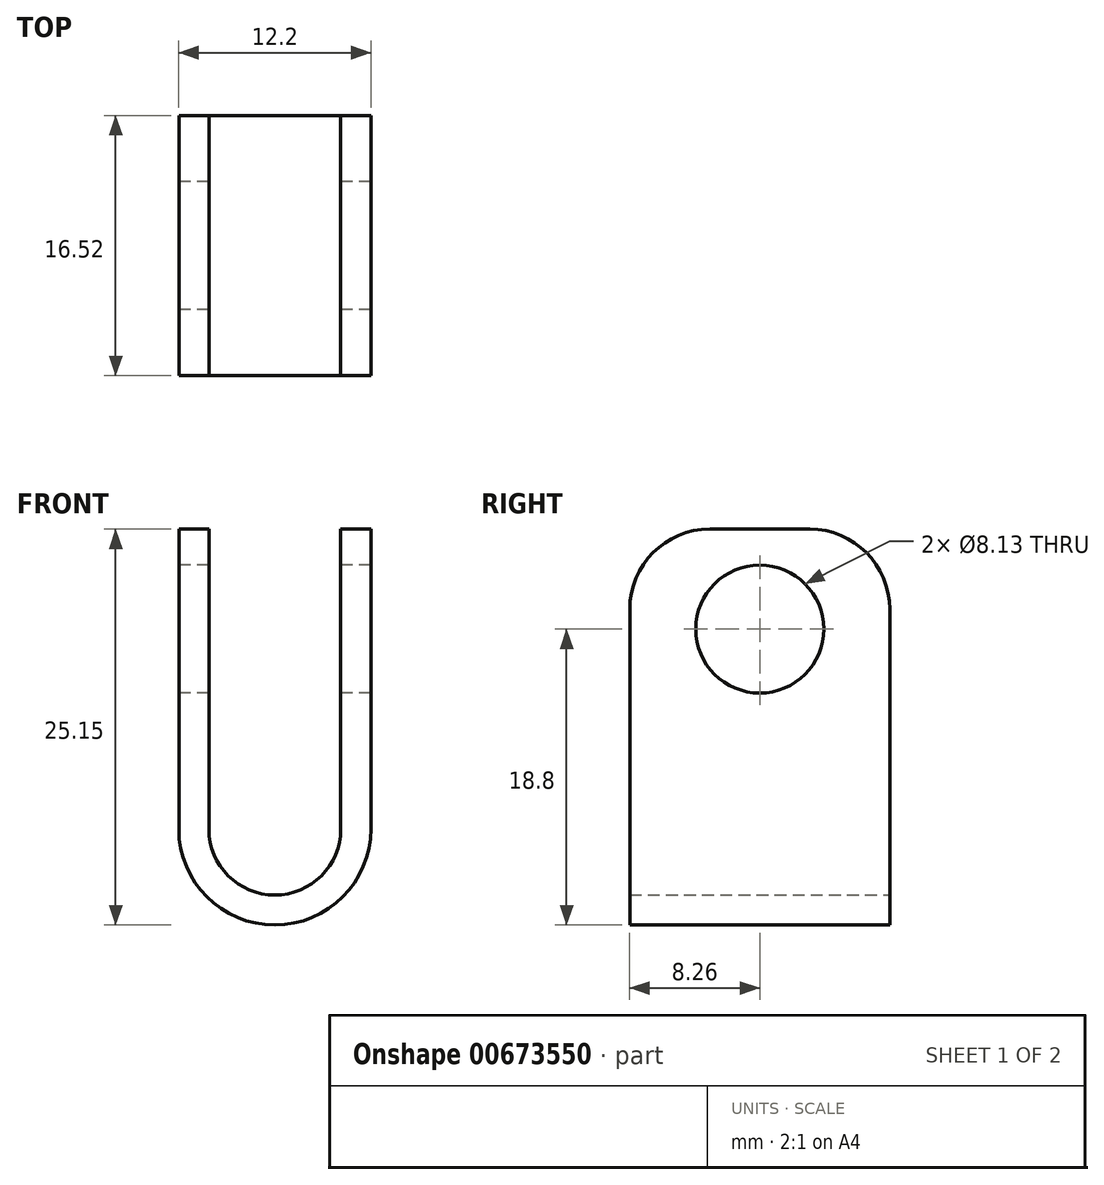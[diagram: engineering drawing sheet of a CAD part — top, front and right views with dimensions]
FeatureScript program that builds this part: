
annotation { "Feature Type Name" : "Feature", "Feature Type Description" : "" }
export const myFeature = defineFeature(function(context is Context, id is Id, definition is map)
    precondition{}
    {
        {
            var Q0;
            Q0=qCreatedBy(makeId("Front.planeOp"),FACE);
            var sketch = newSketch(context, id + "F0", { "sketchPlane" : qUnion([Q0])});
            skArc(sketch, "E0", {"start": v(-4.2, 0) * mm, "mid": v(0, -4.2) * mm, "end": v(4.2, 0) * mm});
            skArc(sketch, "E1", {"start": v(-6.1, 0) * mm, "mid": v(0, -6.1) * mm, "end": v(6.1, 0) * mm});
            skLineSegment(sketch, "E2", {"start": v(-6.1, 0) * mm, "end": v(-6.1, 19.05) * mm});
            skLineSegment(sketch, "E3", {"start": v(6.1, 19.05) * mm, "end": v(6.1, 0) * mm});
            skLineSegment(sketch, "E4", {"start": v(-4.2, 0) * mm, "end": v(-4.2, 19.05) * mm});
            skLineSegment(sketch, "E5", {"start": v(4.2, 0) * mm, "end": v(4.2, 19.05) * mm});
            skLineSegment(sketch, "E6", {"start": v(4.2, 19.05) * mm, "end": v(6.1, 19.05) * mm});
            skLineSegment(sketch, "E7", {"start": v(-6.1, 19.05) * mm, "end": v(-4.2, 19.05) * mm});
            skSolve(sketch);
        }
        {
            var Q0;
            Q0=qSketchRegion(id+"F0",true);
            extrude(context, id + "F1", {"entities" : qUnion([Q0]), "endBound" : BoundingType.SYMMETRIC, "depth" : 16.5 * mm, "offsetDistance" : 25.4 * mm});
        }
        {
            var Q0;
            Q0=makeQuery(id+"F1.opExtrude","CAP_EDGE",EDGE,{"disambiguationData":[OSD([sQuery(id+"F0.wireOp",EDGE,"E6")])],"isStart":false});
            var Q1;
            Q1=makeQuery(id+"F1.opExtrude","CAP_EDGE",EDGE,{"disambiguationData":[OSD([sQuery(id+"F0.wireOp",EDGE,"E6")])],"isStart":true});
            var Q2;
            Q2=makeQuery(id+"F1.opExtrude","CAP_EDGE",EDGE,{"disambiguationData":[OSD([sQuery(id+"F0.wireOp",EDGE,"E7")])],"isStart":true});
            var Q3;
            Q3=makeQuery(id+"F1.opExtrude","CAP_EDGE",EDGE,{"disambiguationData":[OSD([sQuery(id+"F0.wireOp",EDGE,"E7")])],"isStart":false});
            fillet(context, id + "F2", {"entities" : qUnion([Q0, Q1, Q2, Q3]), "radius" : 5.08 * mm, "tangentPropagation" : true, "allowEdgeOverflow" : false});
        }
        {
            var Q0;
            Q0=qCreatedBy(makeId("Right.planeOp"),FACE);
            var sketch = newSketch(context, id + "F3", { "sketchPlane" : qUnion([Q0])});
            skCircle(sketch, "E8", {"center": v(0, 12.7) * mm, "radius": 4.06 * mm});
            skSolve(sketch);
        }
        {
            var Q0;
            Q0=qSketchRegion(id+"F3",true);
            extrude(context, id + "F4", {"entities" : qUnion([Q0]), "operationType" : NewBodyOperationType.REMOVE, "endBound" : BoundingType.THROUGH_ALL, "depth" : 25.4 * mm, "offsetDistance" : 25.4 * mm, "hasSecondDirection" : true, "secondDirectionBound" : SecondDirectionBoundingType.THROUGH_ALL, "secondDirectionOppositeDirection" : true, "secondDirectionDepth" : 25.4 * mm});
        }
    });
